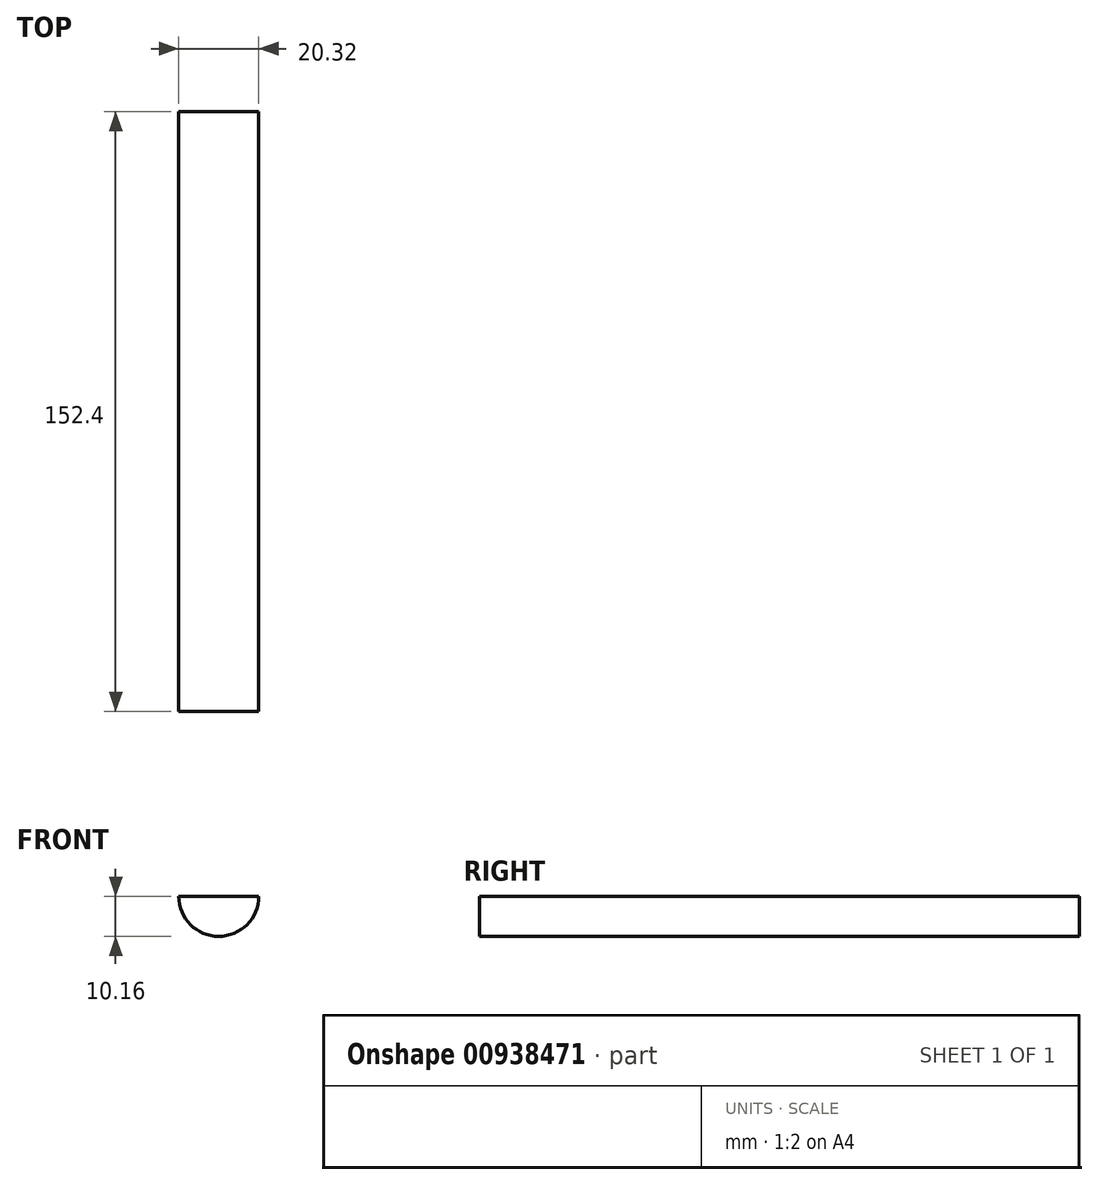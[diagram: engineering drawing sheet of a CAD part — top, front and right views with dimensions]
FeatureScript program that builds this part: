
annotation { "Feature Type Name" : "Feature", "Feature Type Description" : "" }
export const myFeature = defineFeature(function(context is Context, id is Id, definition is map)
    precondition{}
    {
        {
            var Q0;
            Q0=qCreatedBy(makeId("Front.planeOp"),FACE);
            var sketch = newSketch(context, id + "F0", { "sketchPlane" : qUnion([Q0])});
            skLineSegment(sketch, "E0", {"start": v(-10.16, 0) * mm, "end": v(10.16, 0) * mm});
            skArc(sketch, "E1.MirrorCS", {"start": v(10.16, 0) * mm, "mid": v(0, -10.16) * mm, "end": v(-10.16, 0) * mm});
            skSolve(sketch);
        }
        {
            var Q0;
            Q0=makeQuery(id+"F0.imprint","IMPRINT",FACE,{"disambiguationData":[TD([[makeQuery(id+"F0.imprint","IMPRINT",EDGE,{"derivedFrom":sQuery(id+"F0.wireOp",EDGE,"E0")}),-1.0]])]});
            extrude(context, id + "F1", {"entities" : qUnion([Q0]), "depth" : 152.4 * mm, "offsetDistance" : 25.4 * mm});
        }
    });
